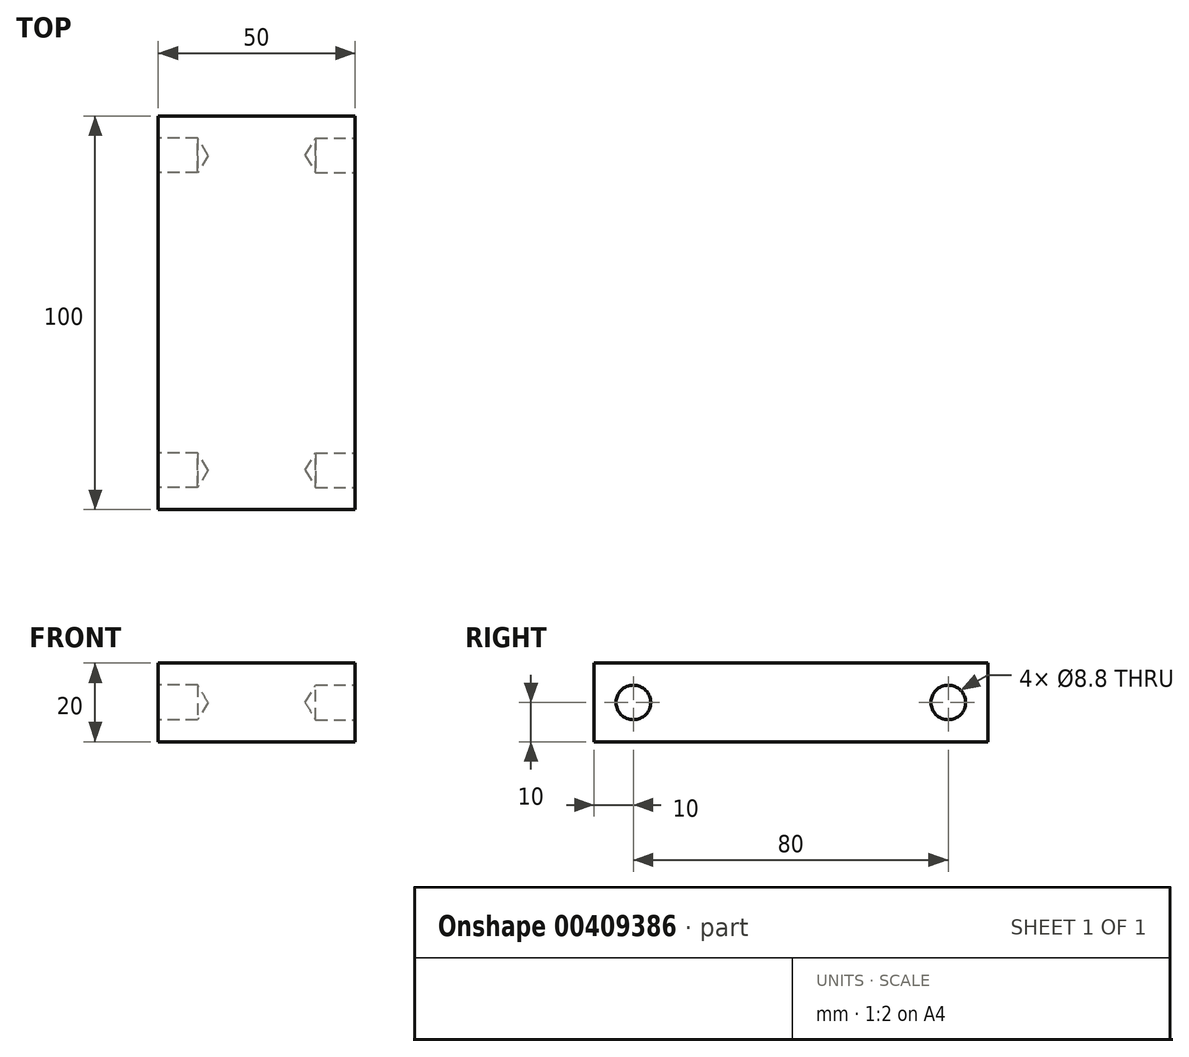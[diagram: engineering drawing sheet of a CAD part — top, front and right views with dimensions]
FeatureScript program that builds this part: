
annotation { "Feature Type Name" : "Feature", "Feature Type Description" : "" }
export const myFeature = defineFeature(function(context is Context, id is Id, definition is map)
    precondition{}
    {
        {
            var Q0;
            Q0=qCreatedBy(makeId("Top.planeOp"),FACE);
            var sketch = newSketch(context, id + "F0", { "sketchPlane" : qUnion([Q0])});
            skLineSegment(sketch, "E0.bottom", {"start": v(25, 50) * mm, "end": v(-25, 50) * mm});
            skLineSegment(sketch, "E0.top", {"start": v(25, -50) * mm, "end": v(-25, -50) * mm});
            skLineSegment(sketch, "E0.left", {"start": v(25, 50) * mm, "end": v(25, -50) * mm});
            skLineSegment(sketch, "E0.right", {"start": v(-25, 50) * mm, "end": v(-25, -50) * mm});
            skPoint(sketch, "E0.middle", {"position": v(0, 0) * mm});
            skSolve(sketch);
        }
        {
            var Q0;
            Q0=makeQuery(id+"F0.imprint","IMPRINT",FACE,{"disambiguationData":[TD([[makeQuery(id+"F0.imprint","IMPRINT",EDGE,{"derivedFrom":sQuery(id+"F0.wireOp",EDGE,"E0.bottom")}),1.0]])]});
            extrude(context, id + "F1", {"entities" : qUnion([Q0]), "depth" : 20 * mm});
        }
        {
            var Q0;
            Q0=makeQuery(id+"F1.opExtrude","SWEPT_FACE",FACE,{"disambiguationData":[OSD([sQuery(id+"F0.wireOp",EDGE,"E0.right")])]});
            var sketch = newSketch(context, id + "F2", { "sketchPlane" : qUnion([Q0])});
            skPoint(sketch, "E1", {"position": v(-40, 10) * mm});
            skPoint(sketch, "E1.positionSnap0", {"position": v(-50, 10) * mm});
            skPoint(sketch, "E2", {"position": v(40, 10) * mm});
            skPoint(sketch, "E2.positionSnap0", {"position": v(50, 10) * mm});
            skSolve(sketch);
        }
        {
            var Q0;
            Q0=makeQuery(id+"F1.opExtrude","SWEPT_FACE",FACE,{"disambiguationData":[OSD([sQuery(id+"F0.wireOp",EDGE,"E0.left")])]});
            var sketch = newSketch(context, id + "F3", { "sketchPlane" : qUnion([Q0])});
            skPoint(sketch, "E3", {"position": v(-40, 10) * mm});
            skPoint(sketch, "E3.positionSnap0", {"position": v(-50, 10) * mm});
            skPoint(sketch, "E4", {"position": v(40, 10) * mm});
            skPoint(sketch, "E4.positionSnap0", {"position": v(50, 10) * mm});
            skSolve(sketch);
        }
        {
            var Q0;
            Q0=sQuery(id+"F3.wireOp",VERTEX,"E3");
            var Q1;
            Q1=sQuery(id+"F3.wireOp",VERTEX,"E4");
            var Q2;
            Q2=sQuery(id+"F2.wireOp",VERTEX,"E1");
            var Q3;
            Q3=sQuery(id+"F2.wireOp",VERTEX,"E2");
            var Q4;
            Q4=makeQuery(id+"F1.opExtrude","SWEPT_BODY",BODY,{"disambiguationData":[OSD([sQuery(id+"F0.wireOp",EDGE,"E0.bottom"),sQuery(id+"F0.wireOp",EDGE,"E0.top"),sQuery(id+"F0.wireOp",EDGE,"E0.left"),sQuery(id+"F0.wireOp",EDGE,"E0.right")])]});
            hole(context, id + "F4", {"style" : HoleStyle.SIMPLE, "endStyle" : HoleEndStyle.BLIND, "standardTappedOrClearance" : lookupTablePath({ "standard" : "ISO", "fit" : "Normal", "size" : "M8", "type" : "Clearance" }), "standardBlindInLast" : lookupTablePath({ "fit" : "Standard", "standard" : "ISO", "size" : "M8", "type" : "Clearance" }), "holeDiameter" : 8.8 * mm, "holeDepth" : 10 * mm, "isTappedThrough" : true, "tappedDepth" : 12 * mm, "tapClearance" : 3, "startFromSketch" : true, "locations" : qUnion([Q0, Q1, Q2, Q3]), "scope" : qUnion([Q4])});
        }
    });
